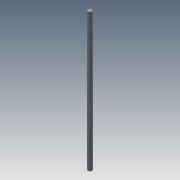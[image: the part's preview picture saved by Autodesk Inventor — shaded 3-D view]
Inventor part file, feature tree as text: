
AUTODESK INVENTOR PART (.ipt)
format: ipt  version: 2013 (Build 170138000, 138)  size: 63,488 bytes
history: native  units: mm
features: sketch x3, extrude x1
ambient origin geometry x8: Origin, YZ Plane, XZ Plane, XY Plane, X Axis, Y Axis, Z Axis, Center Point
bodies: Solid1 (feature_tree)
feature tree (4):
  sketch  "Sketch1"  dims[d1=6.0mm d2=200.0mm d3=0.0mm]
  sketch  "Sketch2"
  extrude  "Extrusion1"  Depth=200.0mm TaperAngle=0.0deg
  sketch  "Sketch3"
